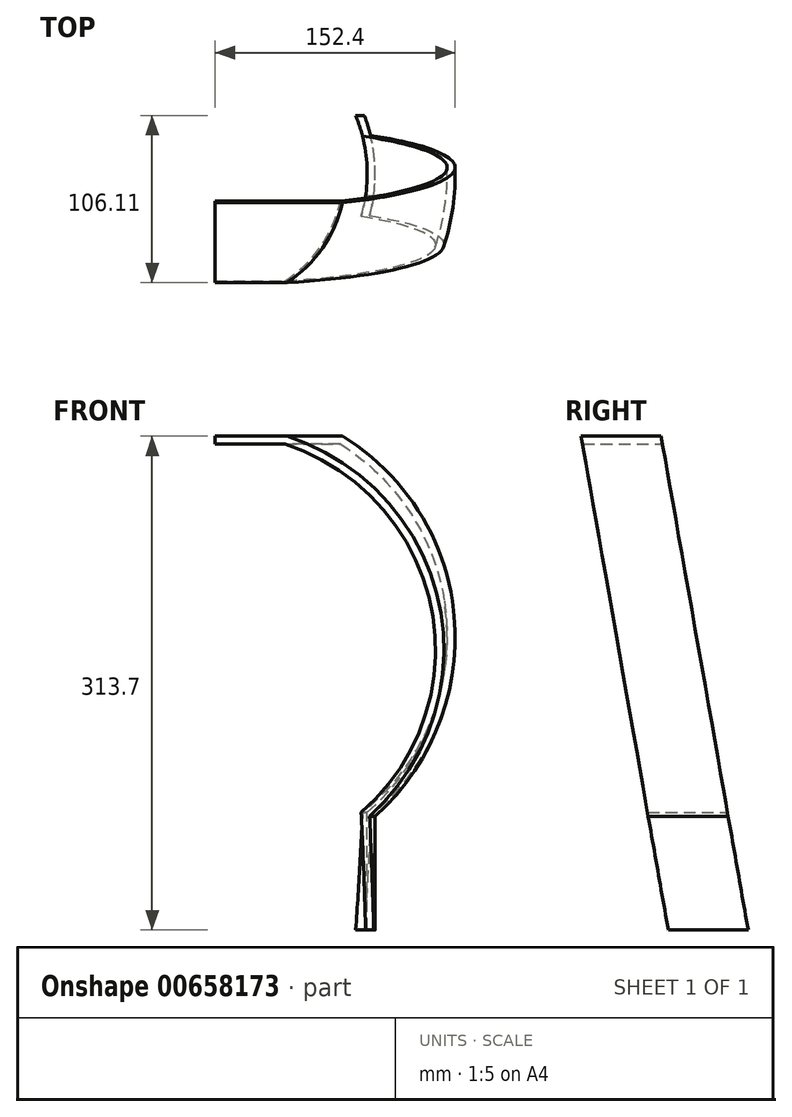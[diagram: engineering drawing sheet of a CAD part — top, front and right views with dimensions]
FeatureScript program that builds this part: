
annotation { "Feature Type Name" : "Feature", "Feature Type Description" : "" }
export const myFeature = defineFeature(function(context is Context, id is Id, definition is map)
    precondition{}
    {
        {
            var Q0;
            Q0=qCreatedBy(makeId("Front.planeOp"),FACE);
            var sketch = newSketch(context, id + "F0", { "sketchPlane" : qUnion([Q0])});
            skLineSegment(sketch, "E0", {"start": v(0, 0) * mm, "end": v(101.6, 0) * mm});
            skLineSegment(sketch, "E1", {"start": v(101.6, 0) * mm, "end": v(101.6, 72.27) * mm});
            skArc(sketch, "E2", {"start": v(101.6, 72.27) * mm, "mid": v(151.95, 197.6) * mm, "end": v(82.96, 313.7) * mm});
            skLineSegment(sketch, "E3", {"start": v(0, 313.7) * mm, "end": v(0, 0) * mm});
            skLineSegment(sketch, "E4", {"start": v(0, 313.7) * mm, "end": v(82.96, 313.7) * mm});
            skPoint(sketch, "E5.orphan", {"position": v(0, 338.26) * mm});
            skSolve(sketch);
        }
        {
            var Q0;
            Q0=makeQuery(id+"F0.imprint","IMPRINT",FACE,{"disambiguationData":[TD([[makeQuery(id+"F0.imprint","IMPRINT",EDGE,{"derivedFrom":sQuery(id+"F0.wireOp",EDGE,"E0")}),1.0]])]});
            var Q1;
            Q1=sQuery(id+"F0.wireOp",EDGE,"E3");
            revolve(context, id + "F1", {"entities" : qUnion([Q0]), "axis" : qUnion([Q1]), "revolveType" : RevolveType.FULL});
        }
        {
            var Q0;
            Q0=makeQuery(id+"F1.opRevolve","SWEPT_FACE",FACE,{"disambiguationData":[OSD([sQuery(id+"F0.wireOp",EDGE,"E0")])]});
            shell(context, id + "F2", {"entities" : qUnion([Q0]), "thickness" : 5.08 * mm});
        }
        {
            var Q0;
            Q0=qCreatedBy(makeId("Right.planeOp"),FACE);
            cPlane(context, id + "F3", {"entities" : qUnion([Q0]), "cplaneType" : CPlaneType.OFFSET, "offset" : 177.8 * mm, "width" : 152.4 * mm, "height" : 152.4 * mm});
        }
        {
            var Q0;
            Q0=qCreatedBy(id+"F3.planeOp",FACE);
            var sketch = newSketch(context, id + "F4", { "sketchPlane" : qUnion([Q0])});
            skLineSegment(sketch, "E6", {"start": v(-73.36, 336.94) * mm, "end": v(-10.27, -20.85) * mm});
            skLineSegment(sketch, "E7", {"start": v(-40.08, -20.85) * mm, "end": v(-168.3, -20.85) * mm});
            skLineSegment(sketch, "E8", {"start": v(-168.3, -20.85) * mm, "end": v(-168.3, 336.94) * mm});
            skLineSegment(sketch, "E9", {"start": v(-168.3, 336.94) * mm, "end": v(-107.49, 336.94) * mm});
            skLineSegment(sketch, "E10", {"start": v(40.53, -20.85) * mm, "end": v(-22.56, 336.94) * mm});
            skLineSegment(sketch, "E11", {"start": v(0, 336.94) * mm, "end": v(175.84, 336.94) * mm});
            skLineSegment(sketch, "E12", {"start": v(175.84, 336.94) * mm, "end": v(175.84, -20.85) * mm});
            skLineSegment(sketch, "E13", {"start": v(175.84, -20.85) * mm, "end": v(62.6, -20.85) * mm});
            skLineSegment(sketch, "E14", {"start": v(0, 336.94) * mm, "end": v(-10.27, 381.58) * mm});
            skLineSegment(sketch, "E15", {"start": v(-10.27, 381.58) * mm, "end": v(-100.43, 381.58) * mm});
            skLineSegment(sketch, "E16", {"start": v(-100.43, 381.58) * mm, "end": v(-107.49, 336.94) * mm});
            skLineSegment(sketch, "E17", {"start": v(-73.36, 336.94) * mm, "end": v(-22.56, 336.94) * mm});
            skLineSegment(sketch, "E18", {"start": v(62.6, -20.85) * mm, "end": v(48.46, -49.56) * mm});
            skLineSegment(sketch, "E19", {"start": v(48.46, -49.56) * mm, "end": v(-22.56, -49.56) * mm});
            skLineSegment(sketch, "E20", {"start": v(-22.56, -49.56) * mm, "end": v(-40.08, -20.85) * mm});
            skLineSegment(sketch, "E21", {"start": v(-10.27, -20.85) * mm, "end": v(40.53, -20.85) * mm});
            skSolve(sketch);
        }
        {
            var Q0;
            Q0=makeQuery(id+"F4.imprint","IMPRINT",FACE,{"disambiguationData":[TD([[makeQuery(id+"F4.imprint","IMPRINT",EDGE,{"derivedFrom":sQuery(id+"F4.wireOp",EDGE,"E6")}),-1.0]])]});
            extrude(context, id + "F5", {"entities" : qUnion([Q0]), "operationType" : NewBodyOperationType.REMOVE, "oppositeDirection" : true, "depth" : 381 * mm, "offsetDistance" : 25.4 * mm});
        }
        {
            var Q0;
            Q0=qCreatedBy(makeId("Front.planeOp"),FACE);
            var sketch = newSketch(context, id + "F6", { "sketchPlane" : qUnion([Q0])});
            skLineSegment(sketch, "E22.bottom", {"start": v(0, 340.04) * mm, "end": v(-183.98, 340.04) * mm});
            skLineSegment(sketch, "E22.top", {"start": v(0, -34.66) * mm, "end": v(-183.98, -34.66) * mm});
            skLineSegment(sketch, "E22.left", {"start": v(0, 340.04) * mm, "end": v(0, -34.66) * mm});
            skLineSegment(sketch, "E22.right", {"start": v(-183.98, 340.04) * mm, "end": v(-183.98, -34.66) * mm});
            skSolve(sketch);
        }
        {
            var Q0;
            Q0 = qSketchRegion(id + "F6", true);
            extrude(context, id + "F7", {"entities" : qUnion([Q0]), "operationType" : NewBodyOperationType.REMOVE, "endBound" : BoundingType.SYMMETRIC, "depth" : 254 * mm, "offsetDistance" : 25.4 * mm});
        }
    });
